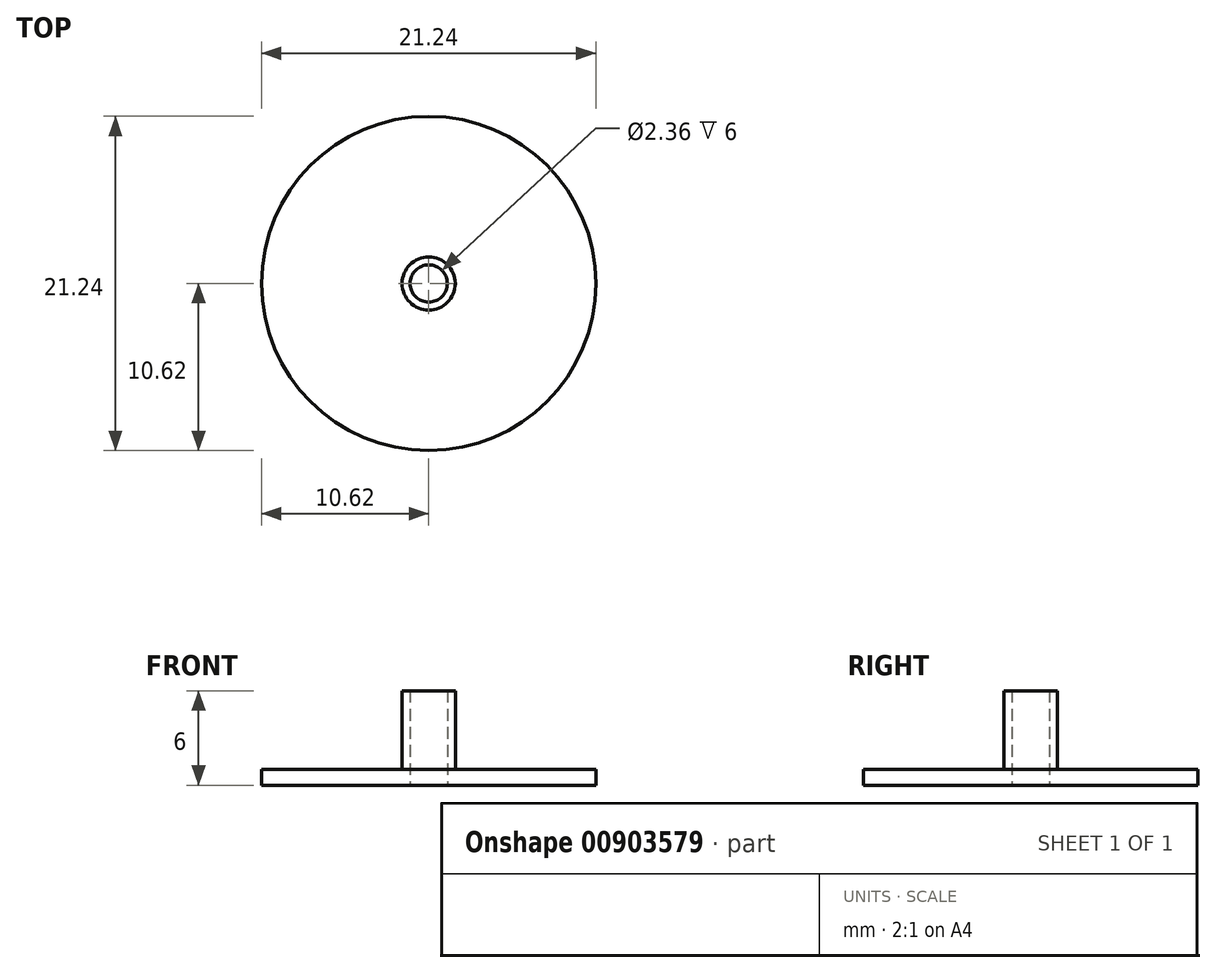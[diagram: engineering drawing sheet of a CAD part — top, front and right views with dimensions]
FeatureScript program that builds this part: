
annotation { "Feature Type Name" : "Feature", "Feature Type Description" : "" }
export const myFeature = defineFeature(function(context is Context, id is Id, definition is map)
    precondition{}
    {
        {
            var Q0;
            Q0=qCreatedBy(makeId("Front.planeOp"),FACE);
            var sketch = newSketch(context, id + "F0", { "sketchPlane" : qUnion([Q0])});
            skLineSegment(sketch, "E0", {"start": v(1.18, 0) * mm, "end": v(10.62, 0) * mm});
            skLineSegment(sketch, "E1", {"start": v(10.62, 0) * mm, "end": v(10.62, 1) * mm});
            skLineSegment(sketch, "E2", {"start": v(10.62, 1) * mm, "end": v(9.62, 1) * mm});
            skLineSegment(sketch, "E3", {"start": v(9.62, 1) * mm, "end": v(9.62, 1) * mm});
            skLineSegment(sketch, "E4", {"start": v(9.62, 1) * mm, "end": v(1.69, 1) * mm});
            skLineSegment(sketch, "E5", {"start": v(1.18, 1) * mm, "end": v(1.18, 0) * mm});
            skLineSegment(sketch, "E6", {"start": v(0, 0) * mm, "end": v(0, 3.05) * mm, "construction": true});
            skLineSegment(sketch, "E7", {"start": v(1.18, 1) * mm, "end": v(1.18, 6) * mm});
            skLineSegment(sketch, "E8", {"start": v(1.18, 6) * mm, "end": v(1.69, 6) * mm});
            skLineSegment(sketch, "E9", {"start": v(1.69, 6) * mm, "end": v(1.69, 1) * mm});
            skSolve(sketch);
        }
        {
            var Q0;
            Q0 = qSketchRegion(id + "F0", true);
            var Q1;
            Q1=sQuery(id+"F0.wireOp",EDGE,"E6");
            revolve(context, id + "F1", {"surfaceOperationType" : NewSurfaceOperationType.NEW, "entities" : qUnion([Q0]), "axis" : qUnion([Q1]), "revolveType" : RevolveType.FULL});
        }
    });
